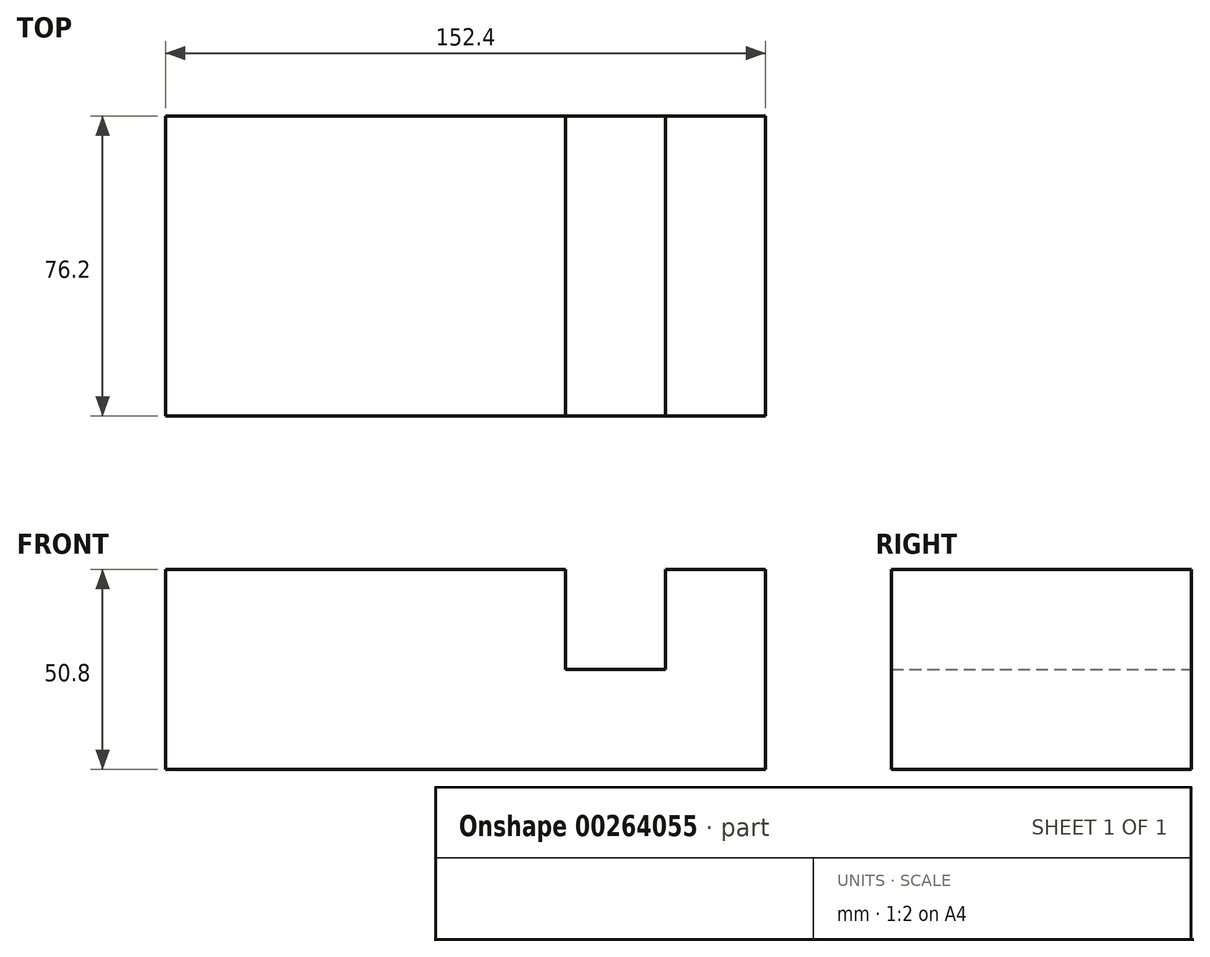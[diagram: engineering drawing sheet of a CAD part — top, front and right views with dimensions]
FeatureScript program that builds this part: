
annotation { "Feature Type Name" : "Feature", "Feature Type Description" : "" }
export const myFeature = defineFeature(function(context is Context, id is Id, definition is map)
    precondition{}
    {
        {
            var Q0;
            Q0=qCreatedBy(makeId("Front.planeOp"),FACE);
            var sketch = newSketch(context, id + "F0", { "sketchPlane" : qUnion([Q0])});
            skLineSegment(sketch, "E0", {"start": v(-75.79, 0) * mm, "end": v(76.61, 0) * mm});
            skLineSegment(sketch, "E1", {"start": v(-75.79, 0) * mm, "end": v(-75.79, 50.8) * mm});
            skLineSegment(sketch, "E2", {"start": v(-75.79, 50.8) * mm, "end": v(25.81, 50.8) * mm});
            skLineSegment(sketch, "E3", {"start": v(25.81, 50.8) * mm, "end": v(25.81, 25.4) * mm});
            skLineSegment(sketch, "E4", {"start": v(25.81, 25.4) * mm, "end": v(51.21, 25.4) * mm});
            skLineSegment(sketch, "E5", {"start": v(51.21, 25.4) * mm, "end": v(51.21, 50.8) * mm});
            skLineSegment(sketch, "E6", {"start": v(51.21, 50.8) * mm, "end": v(76.61, 50.8) * mm});
            skLineSegment(sketch, "E7", {"start": v(76.61, 50.8) * mm, "end": v(76.61, 0) * mm});
            skSolve(sketch);
        }
        {
            var Q0;
            Q0=makeQuery(id+"F0.imprint","IMPRINT",FACE,{"disambiguationData":[TD([[makeQuery(id+"F0.imprint","IMPRINT",EDGE,{"derivedFrom":sQuery(id+"F0.wireOp",EDGE,"E0")}),1.0]])]});
            extrude(context, id + "F1", {"entities" : qUnion([Q0]), "depth" : 76.2 * mm});
        }
    });
